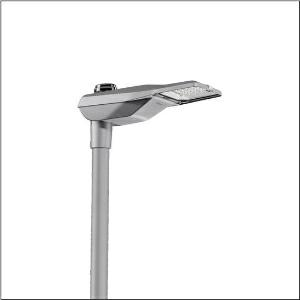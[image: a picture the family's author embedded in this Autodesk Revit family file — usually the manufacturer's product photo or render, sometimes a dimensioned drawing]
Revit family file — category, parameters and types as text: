
# Revit family: streetlight_sl_21_micro___st1_0a_5xe5d27n08db_a8cd
name_source: partatom
category: Lighting Fixtures
units: mm (PartAtom-declared; Revit-internal decimal feet)

## family parameters
Cut with Voids When Loaded = No
Host = Face
Light Source = No
Part Type = Normal
Room Calculation Point = No
Round Connector Dimension = Use Diameter
Shared = No

## types (1)
- --- (1 x LED, 4230 lm, 39.1 W, 2200K)
    Apparent Load = 39 VA
    CIE Flux Codes = 37 72 97 100 100
    Color Rendering = 70
    Color Temperature = 2200K
    Default Elevation = 1800 mm
    Description = Streetlight SL 21 micro, mast luminaire, primary light control with lens, of PMMA, primary optical cover: cover, of toughened safety glass, transparent, light distribution: ST1.0a, light emission: direct distribution, primary light characteristic: asymmetric, installation type: post-top, LED, 3G 1.5mm², High Power LED, rated luminous flux: 4.230lm, luminous efficacy: 108lm/W, light colour: 722, colour temperature: 2200K, control: overheat protection, presetting dimming linear, constant luminous flux control, time-dependent luminous flux control, flexible luminous flux parameterisation, mains connection: 230..240V, AC, 50/60Hz, connection cable pre-assembled, cable length: 6,5m, wiring characteristics: H07RN-F, start of lifetime: 39W, end of service life: 41W, reduction: 18W, luminaire housing, of diecast aluminium (EN AC-44300), powder-coated, Siteco® metallic grey (DB 702S), corrosivity category C5 mid according to DIN EN ISO 12944, multi-level sealing system, sealing non-destructively replaceable, inclination adjustable: 0°, 5°, 10°, 15°, length: 528mm, width: 235mm, height: 110mm, spigot size: 76/60mm (post-top), protection rating (complete): IP66, insulation class (complete): insulation class I (protective earthing), certification: CE, ENEC, ENEC+, VDE, impact resistance: IK09, permissible operating ambient temperature for outdoor applications: -40..+50°C, standard-compliant lighting for roads and squares, packaging unit: 1 piece

Light Distribution: ST1.0a
    Height = 110 mm
    Lamp = 1 x LED
    Lamp Light Flux = 4230 lm
    Lamp Power = 39.1 W
    Lamp count = 1
    Length = 528 mm
    Luminous efficacy = 108 lm/W
    Manufacturer = Siteco
    ModVariant = No
    Model = 5XE5D27N08DB
    Number of Poles = 1
    OnlyDefault = Yes
    Power Factor = 1
    Product Name = Streetlight SL 21 micro | ST1.0a
    Product group = mast luminaire | pylon top
    ProductGroupID = 6100
    Protection Class = Protection class I
    Protection Degree = IP 66
    RLX_Detail_Level = 1
    RLX_Emergency_Light_Flux = 0 lm
    RLX_Emergency_Type = 0
    RLX_Emergency_Type_DB = No
    RlxData = <blob elided: 98505 chars, md5=b0ee258f>
    Socket = socket
    Standby Power = 0 W
    System Light Flux = 4230 lm
    System Power = 39 W
    Type Comments = factory setting: luminous flux: 100 % | dim-lin: 254 | 765 mA
    Type Image = l_1294375.jpg
    URL = http://relux.com
    VarID = @adj_085993
    Voltage = 0 V
    Weight = 0.00 kg
    Width = 235 mm

## geometry (parser evidence)
native form markers: Blend x4, Sweep x9
no freeform markers — native parametric forms only
